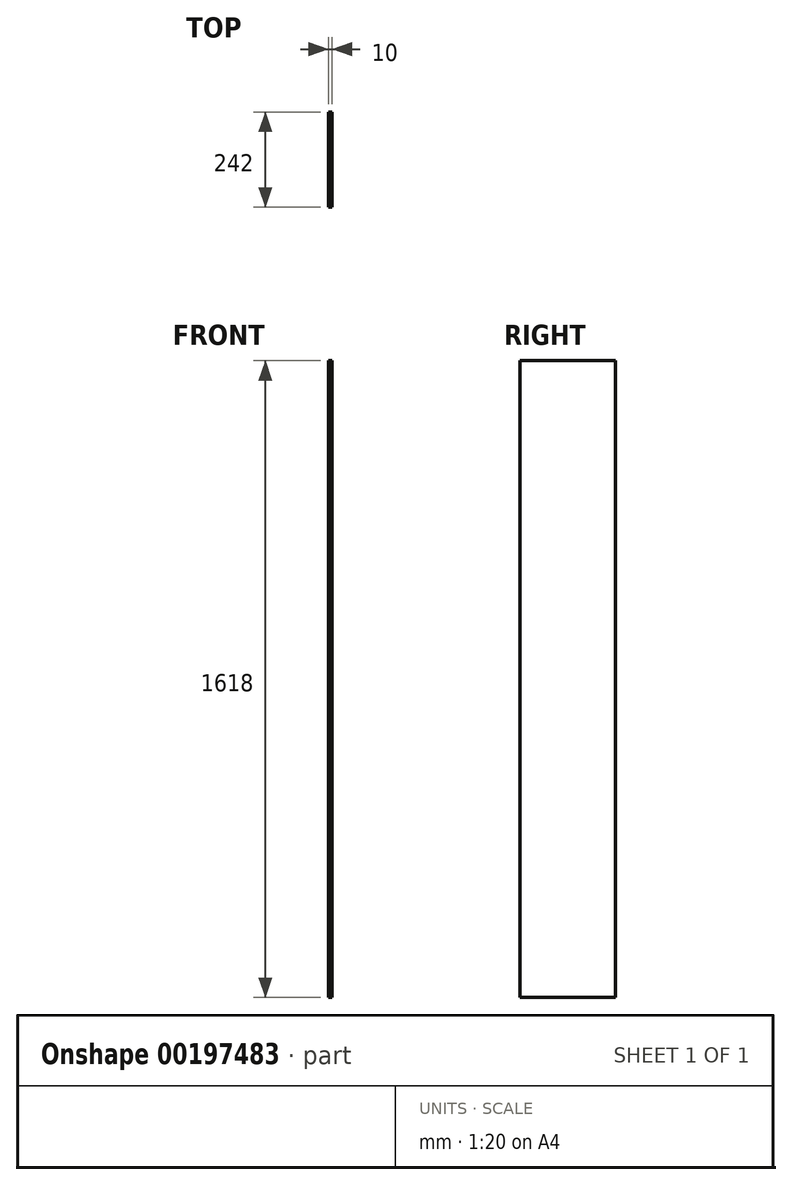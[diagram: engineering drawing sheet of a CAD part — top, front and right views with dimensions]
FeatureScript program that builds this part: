
annotation { "Feature Type Name" : "Feature", "Feature Type Description" : "" }
export const myFeature = defineFeature(function(context is Context, id is Id, definition is map)
    precondition{}
    {
        {
            var Q0;
            Q0=qCreatedBy(makeId("Right.planeOp"),FACE);
            var sketch = newSketch(context, id + "F0", { "sketchPlane" : qUnion([Q0])});
            skLineSegment(sketch, "E0.bottom", {"start": v(121, 809) * mm, "end": v(-121, 809) * mm});
            skLineSegment(sketch, "E0.top", {"start": v(121, -809) * mm, "end": v(-121, -809) * mm});
            skLineSegment(sketch, "E0.left", {"start": v(121, 809) * mm, "end": v(121, -809) * mm});
            skLineSegment(sketch, "E0.right", {"start": v(-121, 809) * mm, "end": v(-121, -809) * mm});
            skPoint(sketch, "E0.middle", {"position": v(0, 0) * mm});
            skSolve(sketch);
        }
        {
            var Q0;
            Q0 = qSketchRegion(id + "F0", true);
            extrude(context, id + "F1", {"entities" : qUnion([Q0]), "depth" : 10 * mm});
        }
    });
